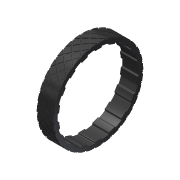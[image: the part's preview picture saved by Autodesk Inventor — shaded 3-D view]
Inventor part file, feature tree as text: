
AUTODESK INVENTOR PART (.ipt)
format: ipt  version: 2013 (Build 170138000, 138)  size: 1,299,456 bytes
history: native  units: in
note: dims shown in document units (in); Inventor stores cm internally (conversion verified against a paired STEP export)
features: pattern_circular x1, extrude x1, mirror x1, imported_body x1, sketch x1
ambient origin geometry x8: Origin, YZ Plane, XZ Plane, XY Plane, X Axis, Y Axis, Z Axis, Center Point
feature tree (5):
  pattern_circular  "CirPattern4"
  extrude  "Extrusion1"  Depth=0.25in TaperAngle=0.0deg
  mirror  "Mirror1"
  imported_body  "Base1"
  sketch  "Sketch1"  dims[d0=8.5in d1=0.25in d2=0.0in]
